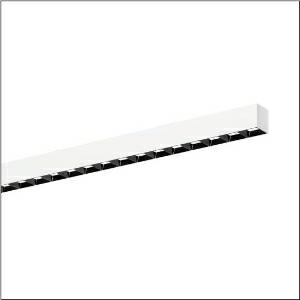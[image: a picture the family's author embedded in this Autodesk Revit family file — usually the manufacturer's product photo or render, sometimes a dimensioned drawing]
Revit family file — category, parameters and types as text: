
# Revit family: silica_21_51mx21da34wb
name_source: partatom
category: Lighting Fixtures
units: mm (PartAtom-declared; Revit-internal decimal feet)

## family parameters
Cut with Voids When Loaded = No
Host = Face
Light Source = No
Part Type = Normal
Room Calculation Point = No
Round Connector Dimension = Use Diameter
Shared = No

## types (1)
- --- (1 x LED, 4320 lm, 27.4 W, 3000K)
    Apparent Load = 27 VA
    CIE Flux Codes = 87 99 100 100 100
    Color Rendering = 80
    Color Temperature = 3000K
    Default Elevation = 1800 mm
    Description = Silica 21, office luminaire, primary light control with darklight reflector, of PMMA, black, CAT 2 (L<= 3000cd/m²), light emission: direct distribution, primary light characteristic: symmetric, installation type: surface-mounted, LED, rated luminous flux: 4.320lm, luminous efficacy: 158lm/W, light colour: 830, colour temperature: 3000K, control gear: DALI 2, with terminal, 3+2-pole, max. 2.5mm², mains connection: 220..240V, AC, 50/60Hz, rated input power: 27.4W, luminaire housing, of aluminium, traffic white (RAL 9016), length: 1.204mm, width: 53mm, height: 53mm, protection rating (complete): IP20, insulation class (complete): insulation class I (protective earthing), certification: CE, permissible operating ambient temperature: 0..+35°C, standard: EN 50419, packaging unit: 1 piece
    Height = 53 mm
    Lamp = 1 x LED
    Lamp Light Flux = 4320 lm
    Lamp Power = 27.4 W
    Lamp count = 1
    Length = 1204 mm
    Luminous efficacy = 158 lm/W
    Manufacturer = Siteco
    ModVariant = No
    Model = 51MX21DA34WB
    Mounting Place = Ceiling
    Mounting Type = Surface mounted
    Number of Poles = 1
    OnlyDefault = Yes
    Power Factor = 1
    Product Name = Silica 21
    Product group = office luminaire | ceiling mounted
    ProductGroupID = 301
    Protection Class = Protection class I
    Protection Degree = IP 20
    RLX_Detail_Level = 1
    RLX_Emergency_Light_Flux = 0 lm
    RLX_Emergency_Type = 0
    RLX_Emergency_Type_DB = No
    RlxData = <blob elided: 41109 chars, md5=7367264c>
    Socket = socket
    Standby Power = 0 W
    System Light Flux = 4320 lm
    System Power = 27 W
    Type Comments = factory setting: luminous flux: 100 % | dim-lin: 254 | 393 mA
    Type Image = l_1335873.jpg
    URL = http://relux.com
    VarID = @adj_028581
    Voltage = 0 V
    Weight = 0.00 kg
    Width = 53 mm

## geometry (parser evidence)
native form markers: Blend x4, Sweep x11
no freeform markers — native parametric forms only
